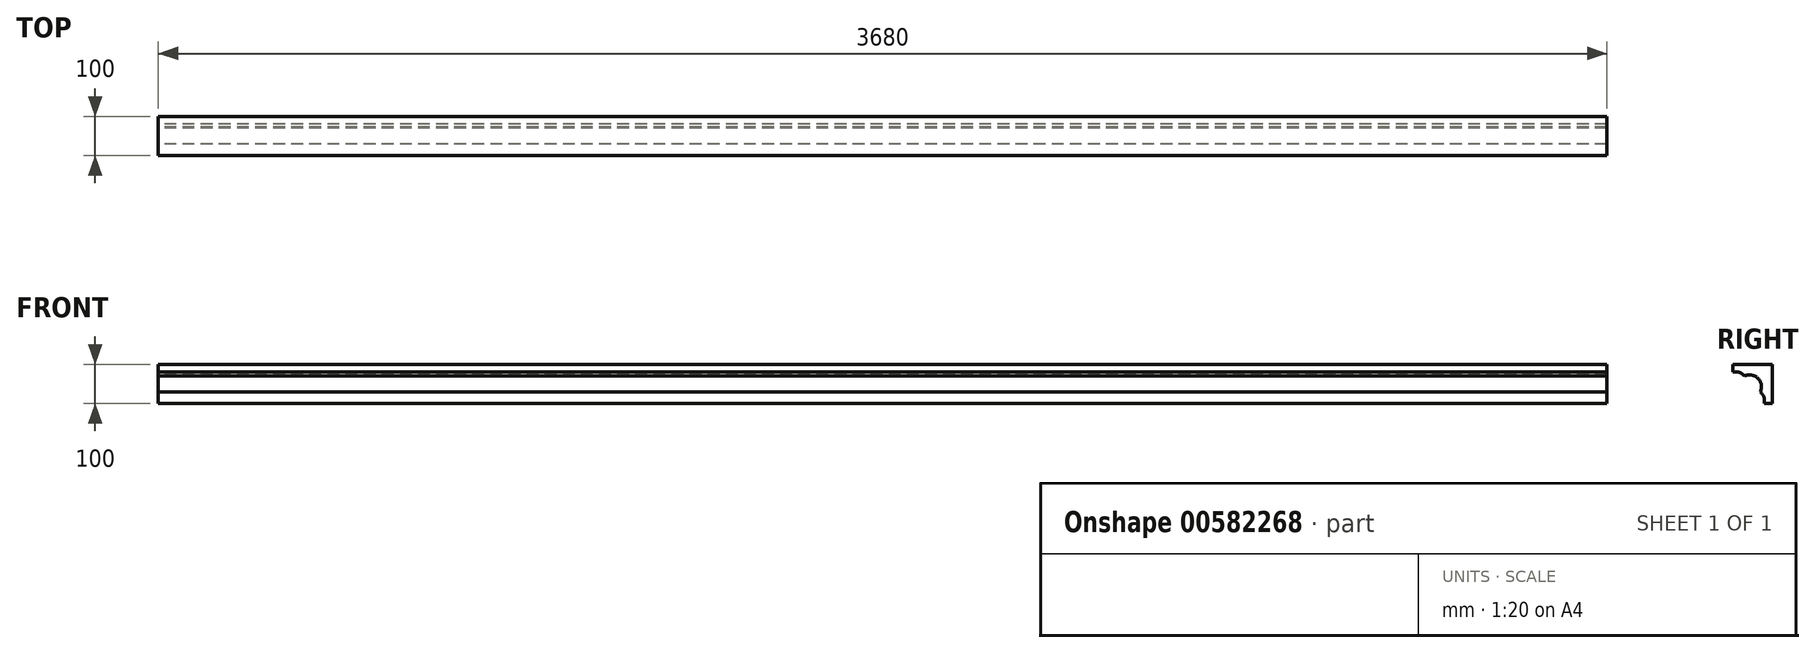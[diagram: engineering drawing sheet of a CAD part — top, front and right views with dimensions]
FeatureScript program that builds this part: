
annotation { "Feature Type Name" : "Feature", "Feature Type Description" : "" }
export const myFeature = defineFeature(function(context is Context, id is Id, definition is map)
    precondition{}
    {
        {
            var Q0;
            Q0=qCreatedBy(makeId("Right.planeOp"),FACE);
            var sketch = newSketch(context, id + "F0", { "sketchPlane" : qUnion([Q0])});
            skLineSegment(sketch, "E0", {"start": v(0, -100) * mm, "end": v(0, 0) * mm});
            skLineSegment(sketch, "E1", {"start": v(0, 0) * mm, "end": v(-100, 0) * mm});
            skLineSegment(sketch, "E2", {"start": v(0, -100) * mm, "end": v(-20, -100) * mm});
            skLineSegment(sketch, "E3", {"start": v(-100, 0) * mm, "end": v(-100, -20) * mm});
            skArc(sketch, "E4", {"start": v(-20, -100) * mm, "mid": v(-20.73, -83.58) * mm, "end": v(-30, -70) * mm});
            skArc(sketch, "E5", {"start": v(-70, -30) * mm, "mid": v(-83.58, -20.73) * mm, "end": v(-100, -20) * mm});
            skArc(sketch, "E6", {"start": v(-30, -70) * mm, "mid": v(-35.86, -35.86) * mm, "end": v(-70, -30) * mm});
            skSolve(sketch);
        }
        {
            var Q0;
            Q0=makeQuery(id+"F0.imprint","IMPRINT",FACE,{"disambiguationData":[TD([[makeQuery(id+"F0.imprint","IMPRINT",EDGE,{"derivedFrom":sQuery(id+"F0.wireOp",EDGE,"E0")}),1.0]])]});
            extrude(context, id + "F1", {"entities" : qUnion([Q0]), "endBound" : BoundingType.SYMMETRIC, "depth" : 3680 * mm, "offsetDistance" : 25 * mm});
        }
    });
